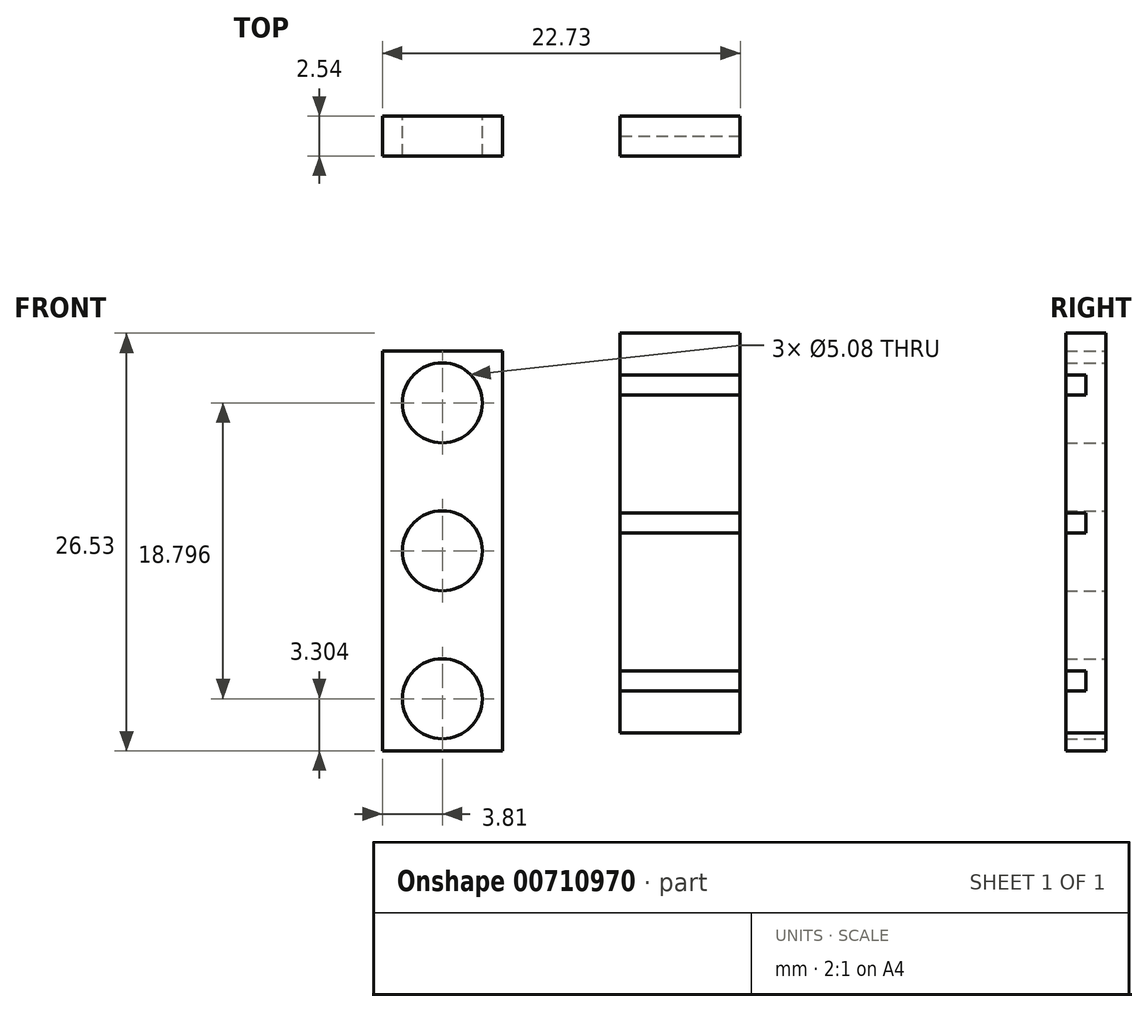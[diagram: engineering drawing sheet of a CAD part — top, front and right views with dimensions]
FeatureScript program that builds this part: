
annotation { "Feature Type Name" : "Feature", "Feature Type Description" : "" }
export const myFeature = defineFeature(function(context is Context, id is Id, definition is map)
    precondition{}
    {
        {
            var Q0;
            Q0=qCreatedBy(makeId("Front.planeOp"),FACE);
            var sketch = newSketch(context, id + "F0", { "sketchPlane" : qUnion([Q0])});
            skLineSegment(sketch, "E0.bottom", {"start": v(-33.8, 23.13) * mm, "end": v(-41.43, 23.13) * mm});
            skLineSegment(sketch, "E0.top", {"start": v(-33.8, 48.53) * mm, "end": v(-41.43, 48.53) * mm});
            skLineSegment(sketch, "E0.left", {"start": v(-33.8, 23.13) * mm, "end": v(-33.8, 48.53) * mm});
            skLineSegment(sketch, "E0.right", {"start": v(-41.43, 23.13) * mm, "end": v(-41.43, 48.53) * mm});
            skPoint(sketch, "E0.middle", {"position": v(-37.62, 35.83) * mm});
            skCircle(sketch, "E1", {"center": v(-37.62, 35.83) * mm, "radius": 2.54 * mm});
            skCircle(sketch, "E2", {"center": v(-37.62, 26.43) * mm, "radius": 2.54 * mm});
            skCircle(sketch, "E3", {"center": v(-37.62, 45.23) * mm, "radius": 2.54 * mm});
            skSolve(sketch);
        }
        {
            var Q0;
            Q0=makeQuery(id+"F0.imprint","IMPRINT",FACE,{"disambiguationData":[TD([[makeQuery(id+"F0.imprint","IMPRINT",EDGE,{"derivedFrom":sQuery(id+"F0.wireOp",EDGE,"E0.bottom")}),-1.0]])]});
            extrude(context, id + "F1", {"entities" : qUnion([Q0]), "depth" : 2.54 * mm, "offsetDistance" : 25.4 * mm});
        }
        {
            var Q0;
            Q0=qCreatedBy(makeId("Front.planeOp"),FACE);
            var sketch = newSketch(context, id + "F2", { "sketchPlane" : qUnion([Q0])});
            skLineSegment(sketch, "E4.bottom", {"start": v(-18.7, 49.66) * mm, "end": v(-26.32, 49.66) * mm});
            skLineSegment(sketch, "E4.top", {"start": v(-18.7, 24.26) * mm, "end": v(-26.32, 24.26) * mm});
            skLineSegment(sketch, "E4.left", {"start": v(-18.7, 49.66) * mm, "end": v(-18.7, 24.26) * mm});
            skLineSegment(sketch, "E4.right", {"start": v(-26.32, 49.66) * mm, "end": v(-26.32, 24.26) * mm});
            skPoint(sketch, "E4.middle", {"position": v(-22.51, 36.96) * mm});
            skLineSegment(sketch, "E5", {"start": v(-26.32, 47) * mm, "end": v(-18.7, 47) * mm});
            skLineSegment(sketch, "E6", {"start": v(-26.32, 45.72) * mm, "end": v(-18.7, 45.72) * mm});
            skLineSegment(sketch, "E7", {"start": v(-26.32, 37.6) * mm, "end": v(-18.7, 37.6) * mm});
            skLineSegment(sketch, "E8", {"start": v(-26.32, 36.32) * mm, "end": v(-18.7, 36.32) * mm});
            skLineSegment(sketch, "E9", {"start": v(-26.32, 28.2) * mm, "end": v(-18.7, 28.2) * mm});
            skLineSegment(sketch, "E10", {"start": v(-26.32, 26.93) * mm, "end": v(-18.7, 26.93) * mm});
            skSolve(sketch);
        }
        {
            var Q0;
            {var subQ0=sQuery(id+"F2.wireOp",EDGE,"E4.bottom");Q0=makeQuery(id+"F2.imprint","IMPRINT",FACE,{"disambiguationData":[TD([[makeQuery(id+"F2.imprint","IMPRINT",EDGE,{"derivedFrom":subQ0}),1.0]])]});}
            var Q1;
            {var subQ0=sQuery(id+"F2.wireOp",EDGE,"E6");Q1=makeQuery(id+"F2.imprint","IMPRINT",FACE,{"disambiguationData":[TD([[makeQuery(id+"F2.imprint","IMPRINT",EDGE,{"derivedFrom":subQ0}),-1.0]])]});}
            var Q2;
            {var subQ0=sQuery(id+"F2.wireOp",EDGE,"E5");Q2=makeQuery(id+"F2.imprint","IMPRINT",FACE,{"disambiguationData":[TD([[makeQuery(id+"F2.imprint","IMPRINT",EDGE,{"derivedFrom":subQ0}),-1.0]])]});}
            var Q3;
            {var subQ0=sQuery(id+"F2.wireOp",EDGE,"E7");Q3=makeQuery(id+"F2.imprint","IMPRINT",FACE,{"disambiguationData":[TD([[makeQuery(id+"F2.imprint","IMPRINT",EDGE,{"derivedFrom":subQ0}),-1.0]])]});}
            var Q4;
            {var subQ0=sQuery(id+"F2.wireOp",EDGE,"E8");Q4=makeQuery(id+"F2.imprint","IMPRINT",FACE,{"disambiguationData":[TD([[makeQuery(id+"F2.imprint","IMPRINT",EDGE,{"derivedFrom":subQ0}),-1.0]])]});}
            var Q5;
            {var subQ0=sQuery(id+"F2.wireOp",EDGE,"E9");Q5=makeQuery(id+"F2.imprint","IMPRINT",FACE,{"disambiguationData":[TD([[makeQuery(id+"F2.imprint","IMPRINT",EDGE,{"derivedFrom":subQ0}),-1.0]])]});}
            var Q6;
            {var subQ0=sQuery(id+"F2.wireOp",EDGE,"E4.top");Q6=makeQuery(id+"F2.imprint","IMPRINT",FACE,{"disambiguationData":[TD([[makeQuery(id+"F2.imprint","IMPRINT",EDGE,{"derivedFrom":subQ0}),-1.0]])]});}
            extrude(context, id + "F3", {"entities" : qUnion([Q0, Q1, Q2, Q3, Q4, Q5, Q6]), "depth" : 2.54 * mm, "offsetDistance" : 25.4 * mm});
        }
        {
            var Q0;
            Q0=makeQuery(id+"F3.opExtrude","CAP_FACE",FACE,{"disambiguationData":[OSD([sQuery(id+"F2.wireOp",EDGE,"E4.bottom"),sQuery(id+"F2.wireOp",EDGE,"E4.top"),sQuery(id+"F2.wireOp",EDGE,"E4.left"),sQuery(id+"F2.wireOp",EDGE,"E4.right")])],"isStart":false});
            var sketch = newSketch(context, id + "F4", { "sketchPlane" : qUnion([Q0])});
            skLineSegment(sketch, "E11", {"start": v(-26.32, 47) * mm, "end": v(-18.7, 47) * mm});
            skLineSegment(sketch, "E12", {"start": v(-26.32, 45.72) * mm, "end": v(-18.7, 45.72) * mm});
            skLineSegment(sketch, "E13", {"start": v(-26.32, 38.23) * mm, "end": v(-18.7, 38.23) * mm});
            skLineSegment(sketch, "E14", {"start": v(-26.32, 36.96) * mm, "end": v(-18.7, 36.96) * mm});
            skLineSegment(sketch, "E15", {"start": v(-26.32, 28.2) * mm, "end": v(-18.7, 28.2) * mm});
            skLineSegment(sketch, "E16", {"start": v(-26.32, 26.93) * mm, "end": v(-18.7, 26.93) * mm});
            skSolve(sketch);
        }
        {
            var Q0;
            {var subQ0=sQuery(id+"F4.wireOp",EDGE,"E11");Q0=makeQuery(id+"F4.imprint","IMPRINT",FACE,{"disambiguationData":[TD([[makeQuery(id+"F4.imprint","IMPRINT",EDGE,{"derivedFrom":subQ0}),-1.0]])]});}
            extrude(context, id + "F5", {"entities" : qUnion([Q0]), "operationType" : NewBodyOperationType.REMOVE, "oppositeDirection" : true, "depth" : 1.27 * mm, "offsetDistance" : 25.4 * mm});
        }
        {
            var Q0;
            {var subQ0=sQuery(id+"F4.wireOp",EDGE,"E13");Q0=makeQuery(id+"F4.imprint","IMPRINT",FACE,{"disambiguationData":[TD([[makeQuery(id+"F4.imprint","IMPRINT",EDGE,{"derivedFrom":subQ0}),-1.0]])]});}
            extrude(context, id + "F6", {"entities" : qUnion([Q0]), "operationType" : NewBodyOperationType.REMOVE, "oppositeDirection" : true, "depth" : 1.27 * mm, "offsetDistance" : 25.4 * mm});
        }
        {
            var Q0;
            {var subQ0=sQuery(id+"F4.wireOp",EDGE,"E15");Q0=makeQuery(id+"F4.imprint","IMPRINT",FACE,{"disambiguationData":[TD([[makeQuery(id+"F4.imprint","IMPRINT",EDGE,{"derivedFrom":subQ0}),-1.0]])]});}
            extrude(context, id + "F7", {"entities" : qUnion([Q0]), "operationType" : NewBodyOperationType.REMOVE, "oppositeDirection" : true, "depth" : 1.27 * mm, "offsetDistance" : 25.4 * mm});
        }
    });
